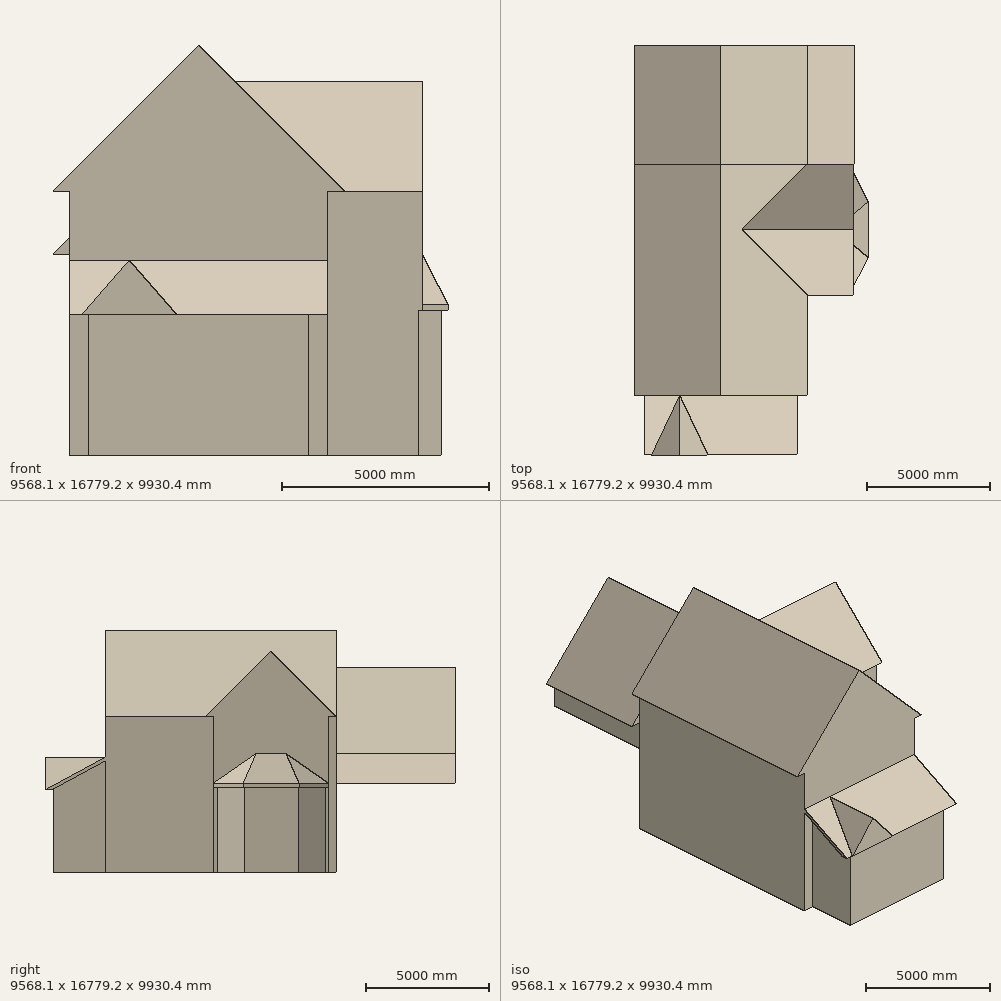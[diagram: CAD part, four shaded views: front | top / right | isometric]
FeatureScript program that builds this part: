
annotation { "Feature Type Name" : "Feature", "Feature Type Description" : "" }
export const myFeature = defineFeature(function(context is Context, id is Id, definition is map)
    precondition{}
    {
        {
            var Q0;
            Q0=qCreatedBy(makeId("Front.planeOp"),FACE);
            var sketch = newSketch(context, id + "F0", { "sketchPlane" : qUnion([Q0])});
            skLineSegment(sketch, "E0", {"start": v(-3529.58, 0) * mm, "end": v(0, 3529.58) * mm});
            skLineSegment(sketch, "E1", {"start": v(0, 3529.58) * mm, "end": v(3529.58, 0) * mm});
            skLineSegment(sketch, "E2", {"start": v(3529.58, 0) * mm, "end": v(-3529.58, 0) * mm});
            skLineSegment(sketch, "E3", {"start": v(0, 0) * mm, "end": v(0, 3529.58) * mm, "construction": true});
            skLineSegment(sketch, "E4", {"start": v(-3124.2, 0) * mm, "end": v(-3124.2, -696.38) * mm, "construction": true});
            skLineSegment(sketch, "E5", {"start": v(-3124.2, -696.38) * mm, "end": v(3124.2, -696.38) * mm, "construction": true});
            skLineSegment(sketch, "E6", {"start": v(3124.2, -696.38) * mm, "end": v(3124.2, 0) * mm, "construction": true});
            skSolve(sketch);
        }
        {
            var Q0;
            Q0=makeQuery(id+"F0.imprint","IMPRINT",FACE,{"disambiguationData":[TD([[makeQuery(id+"F0.imprint","IMPRINT",EDGE,{"derivedFrom":sQuery(id+"F0.wireOp",EDGE,"E0")}),-1.0]])]});
            extrude(context, id + "F1", {"entities" : qUnion([Q0]), "oppositeDirection" : true, "depth" : 9448.8 * mm, "offsetDistance" : 30.48 * mm});
        }
        {
            var Q0;
            Q0=makeQuery(id+"F1.opExtrude","CAP_FACE",FACE,{"disambiguationData":[OSD([sQuery(id+"F0.wireOp",EDGE,"E0"),sQuery(id+"F0.wireOp",EDGE,"E1"),sQuery(id+"F0.wireOp",EDGE,"E2")])],"isStart":false});
            var sketch = newSketch(context, id + "F2", { "sketchPlane" : qUnion([Q0])});
            skLineSegment(sketch, "E7", {"start": v(3529.58, -1524) * mm, "end": v(0, 2005.58) * mm});
            skLineSegment(sketch, "E8", {"start": v(0, 2005.58) * mm, "end": v(-3529.58, -1524) * mm});
            skLineSegment(sketch, "E9", {"start": v(0, 2005.58) * mm, "end": v(0, 3529.58) * mm, "construction": true});
            skLineSegment(sketch, "E10", {"start": v(3529.58, -1524) * mm, "end": v(3529.58, 0) * mm, "construction": true});
            skLineSegment(sketch, "E11", {"start": v(-3529.58, -1524) * mm, "end": v(3529.58, -1524) * mm, "construction": true});
            skLineSegment(sketch, "E12", {"start": v(-3529.58, -1524) * mm, "end": v(-5468.1, -2735.58) * mm});
            skLineSegment(sketch, "E13", {"start": v(-5468.1, -2735.58) * mm, "end": v(3072.38, -2735.58) * mm});
            skLineSegment(sketch, "E14", {"start": v(3072.38, -2735.58) * mm, "end": v(3072.38, -1524) * mm});
            skLineSegment(sketch, "E15", {"start": v(3072.38, -1524) * mm, "end": v(3529.58, -1524) * mm});
            skLineSegment(sketch, "E16", {"start": v(-5163.3, -2735.58) * mm, "end": v(-5163.3, -2545.08) * mm, "construction": true});
            skLineSegment(sketch, "E17", {"start": v(-3529.58, -1524) * mm, "end": v(-3529.58, 0) * mm, "construction": true});
            skSolve(sketch);
        }
        {
            var Q0;
            Q0 = qSketchRegion(id + "F2", true);
            extrude(context, id + "F3", {"entities" : qUnion([Q0]), "operationType" : NewBodyOperationType.ADD, "depth" : 4876.8 * mm, "offsetDistance" : 30.48 * mm});
        }
        {
            var Q0;
            Q0=makeQuery(id+"F1.opExtrude","SWEPT_FACE",FACE,{"disambiguationData":[OSD([sQuery(id+"F0.wireOp",EDGE,"E2")])]});
            var sketch = newSketch(context, id + "F4", { "sketchPlane" : qUnion([Q0])});
            skLineSegment(sketch, "E18", {"start": v(-3124.2, 0) * mm, "end": v(-3124.2, -9448.8) * mm});
            skLineSegment(sketch, "E19", {"start": v(-3124.2, -9448.8) * mm, "end": v(3124.2, -9448.8) * mm});
            skLineSegment(sketch, "E20", {"start": v(3124.2, -9448.8) * mm, "end": v(3124.2, 0) * mm});
            skLineSegment(sketch, "E21", {"start": v(3124.2, 0) * mm, "end": v(-3124.2, 0) * mm});
            skLineSegment(sketch, "E22", {"start": v(-3124.2, -4724.4) * mm, "end": v(-3529.58, -4724.4) * mm, "construction": true});
            skLineSegment(sketch, "E23", {"start": v(3124.2, -4724.4) * mm, "end": v(3529.58, -4724.4) * mm, "construction": true});
            skSolve(sketch);
        }
        {
            var Q0;
            Q0 = qSketchRegion(id + "F4", true);
            extrude(context, id + "F5", {"entities" : qUnion([Q0]), "operationType" : NewBodyOperationType.ADD, "depth" : 6400.8 * mm, "offsetDistance" : 30.48 * mm});
        }
        {
            var Q0;
            Q0=makeQuery(id+"F5.opExtrude","SWEPT_FACE",FACE,{"disambiguationData":[OSD([sQuery(id+"F4.wireOp",EDGE,"E20")])]});
            var sketch = newSketch(context, id + "F6", { "sketchPlane" : qUnion([Q0])});
            skLineSegment(sketch, "E24", {"start": v(4114.8, 0) * mm, "end": v(6781.8, 2667) * mm});
            skLineSegment(sketch, "E25", {"start": v(6781.8, 2667) * mm, "end": v(9448.8, 0) * mm});
            skLineSegment(sketch, "E26", {"start": v(9448.8, 0) * mm, "end": v(4114.8, 0) * mm});
            skLineSegment(sketch, "E27", {"start": v(6781.8, 0) * mm, "end": v(6781.8, 2667) * mm, "construction": true});
            skSolve(sketch);
        }
        {
            var Q0;
            Q0 = qSketchRegion(id + "F6", true);
            var Q1;
            Q1=makeQuery(id+"F1.opExtrude","SWEPT_FACE",FACE,{"disambiguationData":[OSD([sQuery(id+"F0.wireOp",EDGE,"E1")])]});
            extrude(context, id + "F7", {"entities" : qUnion([Q0]), "operationType" : NewBodyOperationType.ADD, "depth" : 2286 * mm, "offsetDistance" : 30.48 * mm, "hasSecondDirection" : true, "secondDirectionBound" : SecondDirectionBoundingType.UP_TO_SURFACE, "secondDirectionOppositeDirection" : true, "secondDirectionDepth" : 30.48 * mm, "secondDirectionBoundEntityFace" : qUnion([Q1])});
        }
        {
            var Q0;
            {var subQ0=sQuery(id+"F0.wireOp",EDGE,"E1");var subQ1=sQuery(id+"F0.wireOp",EDGE,"E2");Q0=makeQuery(id+"F7.boolean.opBoolean","MERGE",FACE,{"derivedFrom":[makeQuery(id+"F5.boolean.opBoolean","SPLIT",FACE,{"disambiguationData":[TD([makeQuery(id+"F1.opExtrude","SWEPT_FACE",FACE,{"disambiguationData":[OSD([subQ0])]})])],"derivedFrom":makeQuery(id+"F1.opExtrude","SWEPT_FACE",FACE,{"disambiguationData":[OSD([subQ1])]})}),makeQuery(id+"F7.opExtrude","SWEPT_FACE",FACE,{"disambiguationData":[OSD([sQuery(id+"F6.wireOp",EDGE,"E26")])]})]});}
            var sketch = newSketch(context, id + "F8", { "sketchPlane" : qUnion([Q0])});
            skLineSegment(sketch, "E28", {"start": v(5410.2, -4419.6) * mm, "end": v(3124.2, -4419.6) * mm});
            skLineSegment(sketch, "E29", {"start": v(3124.2, -4419.6) * mm, "end": v(3124.2, -9144) * mm});
            skLineSegment(sketch, "E30", {"start": v(3124.2, -9144) * mm, "end": v(5410.2, -9144) * mm});
            skLineSegment(sketch, "E31", {"start": v(5410.2, -9144) * mm, "end": v(5410.2, -4419.6) * mm});
            skPoint(sketch, "E32.endSnap0", {"position": v(4267.2, -9144) * mm});
            skLineSegment(sketch, "E33", {"start": v(4267.2, -9448.8) * mm, "end": v(4267.2, -4114.8) * mm, "construction": true});
            skLineSegment(sketch, "E34", {"start": v(4267.2, -6781.8) * mm, "end": v(5410.2, -6781.8) * mm, "construction": true});
            skSolve(sketch);
        }
        {
            var Q0;
            Q0 = qSketchRegion(id + "F8", true);
            var Q1;
            Q1=makeQuery(id+"F5.opExtrude","CAP_FACE",FACE,{"disambiguationData":[OSD([sQuery(id+"F4.wireOp",EDGE,"E18"),sQuery(id+"F4.wireOp",EDGE,"E19"),sQuery(id+"F4.wireOp",EDGE,"E20"),sQuery(id+"F4.wireOp",EDGE,"E21")])],"isStart":false});
            extrude(context, id + "F9", {"entities" : qUnion([Q0]), "operationType" : NewBodyOperationType.ADD, "endBound" : BoundingType.UP_TO_SURFACE, "depth" : 30.48 * mm, "endBoundEntityFace" : qUnion([Q1]), "offsetDistance" : 30.48 * mm});
        }
        {
            var Q0;
            {var subQ0=sQuery(id+"F4.wireOp",EDGE,"E21");var subQ1=sQuery(id+"F4.wireOp",EDGE,"E20");Q0=makeQuery(id+"F12.boolean.opBoolean","MERGE",FACE,{"derivedFrom":[makeQuery(id+"F9.boolean.opBoolean","SPLIT",FACE,{"disambiguationData":[TD([makeQuery(id+"F5.opExtrude","SWEPT_FACE",FACE,{"disambiguationData":[OSD([subQ0])]})])],"derivedFrom":makeQuery(id+"F5.opExtrude","SWEPT_FACE",FACE,{"disambiguationData":[OSD([subQ1])]})}),makeQuery(id+"F12.opExtrude","CAP_FACE",FACE,{"disambiguationData":[OSD([sQuery(id+"F11.wireOp",EDGE,"E35"),sQuery(id+"F11.wireOp",EDGE,"E36"),sQuery(id+"F11.wireOp",EDGE,"E37"),sQuery(id+"F11.wireOp",EDGE,"E38"),sQuery(id+"F11.wireOp",EDGE,"E40")])],"isStart":true})]});}
            cPlane(context, id + "F10", {"entities" : qUnion([Q0]), "cplaneType" : CPlaneType.OFFSET, "offset" : 457.2 * mm, "oppositeDirection" : true, "width" : 152.4 * mm, "height" : 152.4 * mm});
        }
        {
            var Q0;
            Q0=qCreatedBy(id+"F10.planeOp",FACE);
            var sketch = newSketch(context, id + "F11", { "sketchPlane" : qUnion([Q0])});
            skLineSegment(sketch, "E35", {"start": v(0, -1676.4) * mm, "end": v(-2412.07, -2982.94) * mm});
            skLineSegment(sketch, "E36", {"start": v(-2412.07, -2982.94) * mm, "end": v(-2133.6, -2982.94) * mm});
            skLineSegment(sketch, "E37", {"start": v(-2133.6, -2982.94) * mm, "end": v(-2133.6, -6400.8) * mm});
            skLineSegment(sketch, "E38", {"start": v(-2133.6, -6400.8) * mm, "end": v(0, -6400.8) * mm});
            skLineSegment(sketch, "E39", {"start": v(-304.8, -1841.5) * mm, "end": v(0, -1841.5) * mm, "construction": true});
            skLineSegment(sketch, "E40", {"start": v(0, -6400.8) * mm, "end": v(0, -1676.4) * mm});
            skSolve(sketch);
        }
        {
            var Q0;
            Q0 = qSketchRegion(id + "F11", true);
            var Q1;
            Q1=makeQuery(id+"F5.opExtrude","SWEPT_FACE",FACE,{"disambiguationData":[OSD([sQuery(id+"F4.wireOp",EDGE,"E18")])]});
            extrude(context, id + "F12", {"entities" : qUnion([Q0]), "operationType" : NewBodyOperationType.ADD, "endBound" : BoundingType.UP_TO_SURFACE, "oppositeDirection" : true, "depth" : 30.48 * mm, "endBoundEntityFace" : qUnion([Q1]), "hasOffset" : true, "offsetDistance" : 457.2 * mm});
        }
        {
            var Q0;
            Q0=makeQuery(id+"F12.opExtrude","CAP_FACE",FACE,{"disambiguationData":[OSD([sQuery(id+"F11.wireOp",EDGE,"E35"),sQuery(id+"F11.wireOp",EDGE,"E36"),sQuery(id+"F11.wireOp",EDGE,"E37"),sQuery(id+"F11.wireOp",EDGE,"E38"),sQuery(id+"F11.wireOp",EDGE,"E40")])],"isStart":true});
            var sketch = newSketch(context, id + "F13", { "sketchPlane" : qUnion([Q0])});
            skLineSegment(sketch, "E41.0", {"start": v(0, -1676.4) * mm, "end": v(-2412.07, -2982.94) * mm});
            skLineSegment(sketch, "E42", {"start": v(-2412.07, -2982.94) * mm, "end": v(-2133.6, -2982.94) * mm});
            skLineSegment(sketch, "E43", {"start": v(-2133.6, -2982.94) * mm, "end": v(0, -1827.24) * mm});
            skLineSegment(sketch, "E44", {"start": v(0, -1827.24) * mm, "end": v(0, -1676.4) * mm});
            skSolve(sketch);
        }
        {
            var Q0;
            Q0 = qSketchRegion(id + "F13", true);
            var Q1;
            Q1=makeQuery(id+"F5.opExtrude","SWEPT_FACE",FACE,{"disambiguationData":[OSD([sQuery(id+"F4.wireOp",EDGE,"E18")])]});
            extrude(context, id + "F14", {"entities" : qUnion([Q0]), "operationType" : NewBodyOperationType.ADD, "depth" : 457.2 * mm, "offsetDistance" : 30.48 * mm, "hasSecondDirection" : true, "secondDirectionBound" : SecondDirectionBoundingType.UP_TO_SURFACE, "secondDirectionOppositeDirection" : true, "secondDirectionDepth" : 30.48 * mm, "secondDirectionBoundEntityFace" : qUnion([Q1])});
        }
        {
            var Q0;
            Q0=makeQuery(id+"F12.opExtrude","SWEPT_FACE",FACE,{"disambiguationData":[OSD([sQuery(id+"F11.wireOp",EDGE,"E37")])]});
            cPlane(context, id + "F15", {"entities" : qUnion([Q0]), "cplaneType" : CPlaneType.OFFSET, "offset" : 320.04 * mm, "width" : 152.4 * mm, "height" : 152.4 * mm});
        }
        {
            var Q0;
            Q0=qCreatedBy(id+"F15.planeOp",FACE);
            var sketch = newSketch(context, id + "F16", { "sketchPlane" : qUnion([Q0])});
            skLineSegment(sketch, "E45", {"start": v(-2819.4, -2982.94) * mm, "end": v(-1676.4, -1676.4) * mm});
            skLineSegment(sketch, "E46", {"start": v(-1676.4, -1676.4) * mm, "end": v(-533.4, -2982.94) * mm});
            skLineSegment(sketch, "E47", {"start": v(-533.4, -2982.94) * mm, "end": v(-2819.4, -2982.94) * mm});
            skLineSegment(sketch, "E48", {"start": v(-1676.4, -2982.94) * mm, "end": v(-1676.4, -1676.4) * mm, "construction": true});
            skSolve(sketch);
        }
        {
            var Q0;
            Q0 = qSketchRegion(id + "F16", true);
            var Q1;
            Q1=makeQuery(id+"F14.boolean.opBoolean","MERGE",FACE,{"derivedFrom":[makeQuery(id+"F12.opExtrude","SWEPT_FACE",FACE,{"disambiguationData":[OSD([sQuery(id+"F11.wireOp",EDGE,"E35")])]}),makeQuery(id+"F14.opExtrude","SWEPT_FACE",FACE,{"disambiguationData":[OSD([sQuery(id+"F13.wireOp",EDGE,"E41.0")])]})]});
            extrude(context, id + "F17", {"entities" : qUnion([Q0]), "operationType" : NewBodyOperationType.ADD, "endBound" : BoundingType.UP_TO_SURFACE, "oppositeDirection" : true, "depth" : 30.48 * mm, "endBoundEntityFace" : qUnion([Q1]), "offsetDistance" : 30.48 * mm});
        }
        {
            var Q0;
            {var subQ0=sQuery(id+"F4.wireOp",EDGE,"E21");var subQ1=sQuery(id+"F4.wireOp",EDGE,"E20");var subQ2=sQuery(id+"F4.wireOp",EDGE,"E19");var subQ3=sQuery(id+"F4.wireOp",EDGE,"E18");Q0=makeQuery(id+"F12.boolean.opBoolean","MERGE",FACE,{"derivedFrom":[makeQuery(id+"F9.boolean.opBoolean","MERGE",FACE,{"derivedFrom":[makeQuery(id+"F5.opExtrude","CAP_FACE",FACE,{"disambiguationData":[OSD([subQ3,subQ2,subQ1,subQ0])],"isStart":false}),makeQuery(id+"F9.opExtrude","CAP_FACE",FACE,{"disambiguationData":[OSD([subQ3,subQ2,subQ1,subQ0])],"isStart":false})]}),makeQuery(id+"F12.opExtrude","SWEPT_FACE",FACE,{"disambiguationData":[OSD([sQuery(id+"F11.wireOp",EDGE,"E38")])]})]});}
            var sketch = newSketch(context, id + "F18", { "sketchPlane" : qUnion([Q0])});
            skLineSegment(sketch, "E49", {"start": v(5410.2, -4419.6) * mm, "end": v(6038.56, -5638.8) * mm});
            skLineSegment(sketch, "E50", {"start": v(6038.56, -5638.8) * mm, "end": v(6038.56, -7924.8) * mm});
            skLineSegment(sketch, "E51", {"start": v(6038.56, -7924.8) * mm, "end": v(5410.2, -9144) * mm});
            skLineSegment(sketch, "E52", {"start": v(5410.2, -9144) * mm, "end": v(5410.2, -4419.6) * mm});
            skLineSegment(sketch, "E53", {"start": v(6038.56, -6781.8) * mm, "end": v(5410.2, -6781.8) * mm, "construction": true});
            skSolve(sketch);
        }
        {
            var Q0;
            Q0 = qSketchRegion(id + "F18", true);
            extrude(context, id + "F19", {"entities" : qUnion([Q0]), "operationType" : NewBodyOperationType.ADD, "oppositeDirection" : true, "depth" : 3657.6 * mm, "offsetDistance" : 30.48 * mm});
        }
        {
            var Q0;
            Q0=makeQuery(id+"F9.opExtrude","SWEPT_FACE",FACE,{"disambiguationData":[OSD([sQuery(id+"F8.wireOp",EDGE,"E28")])]});
            cPlane(context, id + "F20", {"entities" : qUnion([Q0]), "cplaneType" : CPlaneType.OFFSET, "offset" : 1219.2 * mm, "oppositeDirection" : true, "width" : 152.4 * mm, "height" : 152.4 * mm});
        }
        {
            var Q0;
            Q0=qCreatedBy(id+"F20.planeOp",FACE);
            var sketch = newSketch(context, id + "F21", { "sketchPlane" : qUnion([Q0])});
            skLineSegment(sketch, "E54", {"start": v(6038.56, -2743.2) * mm, "end": v(5410.2, -1524) * mm});
            skLineSegment(sketch, "E55", {"start": v(5410.2, -1524) * mm, "end": v(5410.2, -2743.2) * mm});
            skLineSegment(sketch, "E56", {"start": v(5410.2, -2743.2) * mm, "end": v(6038.56, -2743.2) * mm});
            skSolve(sketch);
        }
        {
            var Q0;
            Q0 = qSketchRegion(id + "F21", true);
            extrude(context, id + "F22", {"entities" : qUnion([Q0]), "operationType" : NewBodyOperationType.ADD, "oppositeDirection" : true, "depth" : 2286 * mm, "offsetDistance" : 30.48 * mm});
        }
        {
            var Q0;
            Q0=makeQuery(id+"F19.opExtrude","SWEPT_FACE",FACE,{"disambiguationData":[OSD([sQuery(id+"F18.wireOp",EDGE,"E50")])]});
            var sketch = newSketch(context, id + "F23", { "sketchPlane" : qUnion([Q0])});
            skLineSegment(sketch, "E57", {"start": v(5638.8, -2743.2) * mm, "end": v(6172.2, -1524) * mm});
            skLineSegment(sketch, "E58", {"start": v(6172.2, -1524) * mm, "end": v(5638.8, -1524) * mm});
            skLineSegment(sketch, "E59", {"start": v(5638.8, -1524) * mm, "end": v(5638.8, -2743.2) * mm});
            skLineSegment(sketch, "E60", {"start": v(6781.8, -2743.2) * mm, "end": v(6781.8, -1660.14) * mm, "construction": true});
            skLineSegment(sketch, "E61.MirrorCS", {"start": v(7924.8, -1524) * mm, "end": v(7924.8, -2743.2) * mm});
            skLineSegment(sketch, "E62.MirrorCS", {"start": v(7924.8, -2743.2) * mm, "end": v(7391.4, -1524) * mm});
            skLineSegment(sketch, "E63.MirrorCS", {"start": v(7391.4, -1524) * mm, "end": v(7924.8, -1524) * mm});
            skSolve(sketch);
        }
        {
            var Q0;
            Q0 = qSketchRegion(id + "F23", true);
            var Q1;
            Q1=makeQuery(id+"F9.boolean.opBoolean","MERGE",FACE,{"derivedFrom":[makeQuery(id+"F7.opExtrude","CAP_FACE",FACE,{"disambiguationData":[OSD([sQuery(id+"F6.wireOp",EDGE,"E24"),sQuery(id+"F6.wireOp",EDGE,"E25"),sQuery(id+"F6.wireOp",EDGE,"E26")])],"isStart":false}),makeQuery(id+"F9.opExtrude","SWEPT_FACE",FACE,{"disambiguationData":[OSD([sQuery(id+"F8.wireOp",EDGE,"E31")])]})]});
            extrude(context, id + "F24", {"entities" : qUnion([Q0]), "operationType" : NewBodyOperationType.REMOVE, "endBound" : BoundingType.UP_TO_SURFACE, "oppositeDirection" : true, "depth" : 30.48 * mm, "endBoundEntityFace" : qUnion([Q1]), "offsetDistance" : 30.48 * mm});
        }
        {
            var Q1;
            {var subQ1=sQuery(id+"F18.wireOp",EDGE,"E49");var subQ2=sQuery(id+"F18.wireOp",EDGE,"E50");Q1=makeQuery(id+"F22.boolean.opBoolean","SPLIT",FACE,{"disambiguationData":[TD([makeQuery(id+"F9.opExtrude","SWEPT_FACE",FACE,{"disambiguationData":[OSD([sQuery(id+"F8.wireOp",EDGE,"E28")])]})])],"derivedFrom":makeQuery(id+"F19.opExtrude","CAP_FACE",FACE,{"disambiguationData":[OSD([subQ1,subQ2,sQuery(id+"F18.wireOp",EDGE,"E51"),sQuery(id+"F18.wireOp",EDGE,"E52")])],"isStart":false})});}
            var Q2;
            Q2=makeQuery(id+"F24.boolean.opBoolean","COPY",VERTEX,{"derivedFrom":makeQuery(id+"F24.opExtrude","CAP_VERTEX",VERTEX,{"disambiguationData":[OSD([sQuery(id+"F6.wireOp",EDGE,"E24"),sQuery(id+"F6.wireOp",EDGE,"E25"),sQuery(id+"F6.wireOp",EDGE,"E26"),sQuery(id+"F8.wireOp",EDGE,"E31"),sQuery(id+"F23.wireOp",EDGE,"E57"),sQuery(id+"F23.wireOp",EDGE,"E58")])],"isStart":false})});
            loft(context, id + "F25", {"operationType" : NewBodyOperationType.ADD, "sheetProfilesArray" : [{ "sheetProfileEntities" : qUnion([Q1]) }, { "sheetProfileEntities" : qUnion([Q2]) }]});
        }
        {
            var Q1;
            {var subQ0=sQuery(id+"F18.wireOp",EDGE,"E50");var subQ2=sQuery(id+"F18.wireOp",EDGE,"E51");Q1=makeQuery(id+"F22.boolean.opBoolean","SPLIT",FACE,{"disambiguationData":[TD([makeQuery(id+"F9.opExtrude","SWEPT_FACE",FACE,{"disambiguationData":[OSD([sQuery(id+"F8.wireOp",EDGE,"E30")])]})])],"derivedFrom":makeQuery(id+"F19.opExtrude","CAP_FACE",FACE,{"disambiguationData":[OSD([sQuery(id+"F18.wireOp",EDGE,"E49"),subQ0,subQ2,sQuery(id+"F18.wireOp",EDGE,"E52")])],"isStart":false})});}
            var Q2;
            Q2=makeQuery(id+"F24.boolean.opBoolean","COPY",VERTEX,{"derivedFrom":makeQuery(id+"F24.opExtrude","CAP_VERTEX",VERTEX,{"disambiguationData":[OSD([sQuery(id+"F6.wireOp",EDGE,"E24"),sQuery(id+"F6.wireOp",EDGE,"E25"),sQuery(id+"F6.wireOp",EDGE,"E26"),sQuery(id+"F8.wireOp",EDGE,"E31"),sQuery(id+"F23.wireOp",EDGE,"E62.MirrorCS"),sQuery(id+"F23.wireOp",EDGE,"E63.MirrorCS")])],"isStart":false})});
            loft(context, id + "F26", {"operationType" : NewBodyOperationType.ADD, "sheetProfilesArray" : [{ "sheetProfileEntities" : qUnion([Q1]) }, { "sheetProfileEntities" : qUnion([Q2]) }]});
        }
        {
            var Q0;
            {var subQ0=sQuery(id+"F4.wireOp",EDGE,"E21");var subQ1=sQuery(id+"F4.wireOp",EDGE,"E20");var subQ2=sQuery(id+"F4.wireOp",EDGE,"E19");var subQ3=sQuery(id+"F4.wireOp",EDGE,"E18");Q0=makeQuery(id+"F19.boolean.opBoolean","MERGE",FACE,{"derivedFrom":[makeQuery(id+"F12.boolean.opBoolean","MERGE",FACE,{"derivedFrom":[makeQuery(id+"F9.boolean.opBoolean","MERGE",FACE,{"derivedFrom":[makeQuery(id+"F5.opExtrude","CAP_FACE",FACE,{"disambiguationData":[OSD([subQ3,subQ2,subQ1,subQ0])],"isStart":false}),makeQuery(id+"F9.opExtrude","CAP_FACE",FACE,{"disambiguationData":[OSD([subQ3,subQ2,subQ1,subQ0])],"isStart":false})]}),makeQuery(id+"F12.opExtrude","SWEPT_FACE",FACE,{"disambiguationData":[OSD([sQuery(id+"F11.wireOp",EDGE,"E38")])]})]}),makeQuery(id+"F19.opExtrude","CAP_FACE",FACE,{"disambiguationData":[OSD([sQuery(id+"F18.wireOp",EDGE,"E49"),sQuery(id+"F18.wireOp",EDGE,"E50"),sQuery(id+"F18.wireOp",EDGE,"E51"),sQuery(id+"F18.wireOp",EDGE,"E52")])],"isStart":true})]});}
            var sketch = newSketch(context, id + "F27", { "sketchPlane" : qUnion([Q0])});
            skLineSegment(sketch, "E64.0", {"start": v(5886.16, -7887.84) * mm, "end": v(5317.3, -8991.6) * mm});
            skLineSegment(sketch, "E64.1", {"start": v(5886.16, -5675.76) * mm, "end": v(5886.16, -7887.84) * mm});
            skLineSegment(sketch, "E64.2", {"start": v(5317.3, -4572) * mm, "end": v(5886.16, -5675.76) * mm});
            skLineSegment(sketch, "E65", {"start": v(5317.3, -8991.6) * mm, "end": v(5317.3, -9144) * mm});
            skLineSegment(sketch, "E66", {"start": v(5317.3, -4572) * mm, "end": v(5317.3, -4419.6) * mm});
            skLineSegment(sketch, "E67", {"start": v(5317.3, -4572) * mm, "end": v(5317.3, -8991.6) * mm, "construction": true});
            skLineSegment(sketch, "E68.0", {"start": v(6038.56, -7924.8) * mm, "end": v(5410.2, -9144) * mm});
            skLineSegment(sketch, "E69.0", {"start": v(6038.56, -5638.8) * mm, "end": v(6038.56, -7924.8) * mm});
            skLineSegment(sketch, "E70.0", {"start": v(5410.2, -4419.6) * mm, "end": v(6038.56, -5638.8) * mm});
            skLineSegment(sketch, "E71", {"start": v(5317.3, -4419.6) * mm, "end": v(5410.2, -4419.6) * mm});
            skLineSegment(sketch, "E72", {"start": v(5317.3, -9144) * mm, "end": v(5410.2, -9144) * mm});
            skSolve(sketch);
        }
        {
            var Q0;
            Q0 = qSketchRegion(id + "F27", true);
            var Q1;
            {var subQ0=sQuery(id+"F23.wireOp",EDGE,"E59");var subQ1=sQuery(id+"F23.wireOp",EDGE,"E57");var subQ2=sQuery(id+"F21.wireOp",EDGE,"E56");var subQ3=sQuery(id+"F21.wireOp",EDGE,"E54");var subQ4=sQuery(id+"F18.wireOp",EDGE,"E50");var subQ5=sQuery(id+"F18.wireOp",EDGE,"E49");Q1=makeQuery(id+"F25.boolean.opBoolean","MERGE",VERTEX,{"derivedFrom":[makeQuery(id+"F24.boolean.opBoolean","MERGE",VERTEX,{"derivedFrom":[makeQuery(id+"F22.boolean.opBoolean","MERGE",VERTEX,{"derivedFrom":[makeQuery(id+"F19.opExtrude","CAP_VERTEX",VERTEX,{"disambiguationData":[OSD([subQ5,subQ4])],"isStart":false}),makeQuery(id+"F22.opExtrude","CAP_VERTEX",VERTEX,{"disambiguationData":[OSD([subQ3,subQ2])],"isStart":true})]}),makeQuery(id+"F24.opExtrude","CAP_VERTEX",VERTEX,{"disambiguationData":[OSD([subQ5,subQ4,subQ3,subQ2,subQ1,subQ0])],"isStart":true})]}),makeQuery(id+"F25.opLoft","MID_CAP_VERTEX",VERTEX,{"disambiguationData":[OSD([subQ5,subQ4,subQ3,subQ2,subQ1,subQ0])],"capPos":0.0})]});}
            extrude(context, id + "F28", {"entities" : qUnion([Q0]), "operationType" : NewBodyOperationType.REMOVE, "endBound" : BoundingType.UP_TO_VERTEX, "oppositeDirection" : true, "depth" : 30.48 * mm, "endBoundEntityVertex" : qUnion([Q1]), "hasOffset" : true, "offsetDistance" : 152.4 * mm});
        }
    });
